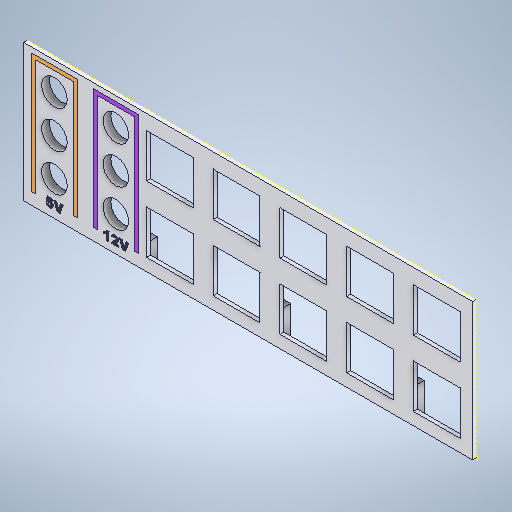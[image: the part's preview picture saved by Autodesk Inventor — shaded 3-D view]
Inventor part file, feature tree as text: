
AUTODESK INVENTOR PART (.ipt)
format: ipt  version: 2025 (Build 290162000, 162)  size: 1,114,624 bytes
history: native  units: in
note: dims shown in document units (in); Inventor stores cm internally (conversion verified against a paired STEP export)
features: projected_geometry x29, sketch x17, extrude x14
ambient origin geometry x8: Origin, YZ Plane, XZ Plane, XY Plane, X Axis, Y Axis, Z Axis, Center Point
bodies: Solid1 (feature_tree), Solid3 (feature_tree), Solid5 (feature_tree)
feature tree (60):
  extrude  "Extrusion1"  Depth=0.25in
  extrude  "Extrusion2"  Depth=0.875in
  extrude  "Extrusion3"  Depth=1.9685in
  extrude  "Extrusion4"  Depth=9.0in
  extrude  "Extrusion5"  Depth=0.0787in TaperAngle=0.0deg
  sketch  "Sketch7"  dims[d51=0.1in d52=0.1in]
  extrude  "Extrusion6"  Depth=0.1in
  extrude  "Extrusion7"  Depth=0.1in
  extrude  "Extrusion8"  Depth=0.1in
  extrude  "Extrusion9"  Depth=0.1in
  extrude  "Extrusion10"  Depth=0.1in
  extrude  "Extrusion11"  Depth=0.515in
  extrude  "Extrusion12"  Depth=0.3937in
  extrude  "Extrusion14"  Depth=0.1in
  extrude  "Extrusion15"  Depth=0.1in
  sketch  "Sketch1"  dims[d0=0.25in d1=0.25in]
  sketch  "Sketch Rectangular Pattern1"  dims[d2=0.9375in d3=0.875in]
  sketch  "Sketch3"  dims[d4=0.2in d5=1.9685in d7=1.3375in d8=0.7874in d10=1.325in]
  projected_geometry  "Projected Loop2"
  sketch  "Sketch Rectangular Pattern3"  dims[d13=2.75in d16=9.0in]
  projected_geometry  "Projected Loop3"
  sketch  "Sketch4"  dims[d17=2.75in d33=0.0787in d34=0.0in]
  projected_geometry  "Projected Loop4"
  sketch  "Sketch5"  dims[d42=0.125in d43=0.125in d44=0.125in d45=0.125in d48=0.1in]
  projected_geometry  "Projected Loop5"
  sketch  "Sketch6"  dims[d49=0.1in d50=0.1in]
  projected_geometry  "Projected Loop6"
  projected_geometry  "Projected Loop7"
  projected_geometry  "Projected Loop8"
  projected_geometry  "Projected Loop9"
  projected_geometry  "Projected Loop10"
  projected_geometry  "Projected Loop11"
  projected_geometry  "Projected Loop12"
  projected_geometry  "Projected Loop13"
  sketch  "Sketch8"  dims[d53=0.1in d54=0.1in]
  projected_geometry  "Projected Loop14"
  sketch  "Sketch9"  dims[d55=0.1in d56=0.1in]
  projected_geometry  "Projected Loop15"
  sketch  "Sketch10"  dims[d57=0.1in d58=0.515in]
  sketch  "Sketch11"  dims[d59=0.5575in d60=1.1811in d62=0.75in d63=0.3937in d65=1.0in]
  projected_geometry  "Projected Loop16"
  sketch  "Sketch13"  dims[d67=0.1in d68=0.1in]
  projected_geometry  "Projected Loop17"
  projected_geometry  "Projected Loop18"
  sketch  "Sketch14"  dims[d69=0.1in d70=0.1in]
  projected_geometry  "Projected Loop19"
  projected_geometry  "Projected Loop20"
  projected_geometry  "Projected Loop21"
  projected_geometry  "Projected Loop22"
  projected_geometry  "Projected Loop23"
  projected_geometry  "Projected Loop24"
  sketch  "Sketch15"  dims[d71=0.1in]
  sketch  "Sketch17"  dims[d72=0.1in]
  projected_geometry  "Projected Loop33"
  projected_geometry  "Projected Loop34"
  projected_geometry  "Projected Loop35"
  projected_geometry  "Projected Loop36"
  projected_geometry  "Projected Loop37"
  sketch  "Sketch18"  dims[d73=0.0787in d74=0.0in d75=0.0787in d76=0.0787in d77=0.0787in d78=0.0in d79=0.0787in d80=0.0787in d81=0.0787in d82=0.0in d83=0.5in d84=0.4in d85=0.2in d86=0.4in d87=0.1575in d88=0.0787in d89=0.0in d90=0.0in d91=1.2875in d92=2.475in d93=2.475in d94=0.1969in d95=0.1969in d96=0.1969in d97=0.1969in d98=0.0787in d99=0.0394in d100=0.0in d101=0.0394in d102=0.0in d103=0.1969in d104=0.1969in d105=0.0787in d106=0.0394in d107=0.0in d108=0.0394in d109=0.0in d110=0.0098in d111=0.0098in d112=0.0098in d113=0.0098in d114=0.0098in d115=0.0098in d116=1.0in d117=0.0in d118=1.0in d119=0.0in d120=0.0394in d121=0.0in d124=0.0394in d125=0.0in d126=0.0098in d127=0.0098in d128=0.0098in d129=0.0098in d130=0.0098in d131=0.0098in d132=1.0in d133=0.0in]
  projected_geometry  "Projected Loop38"
